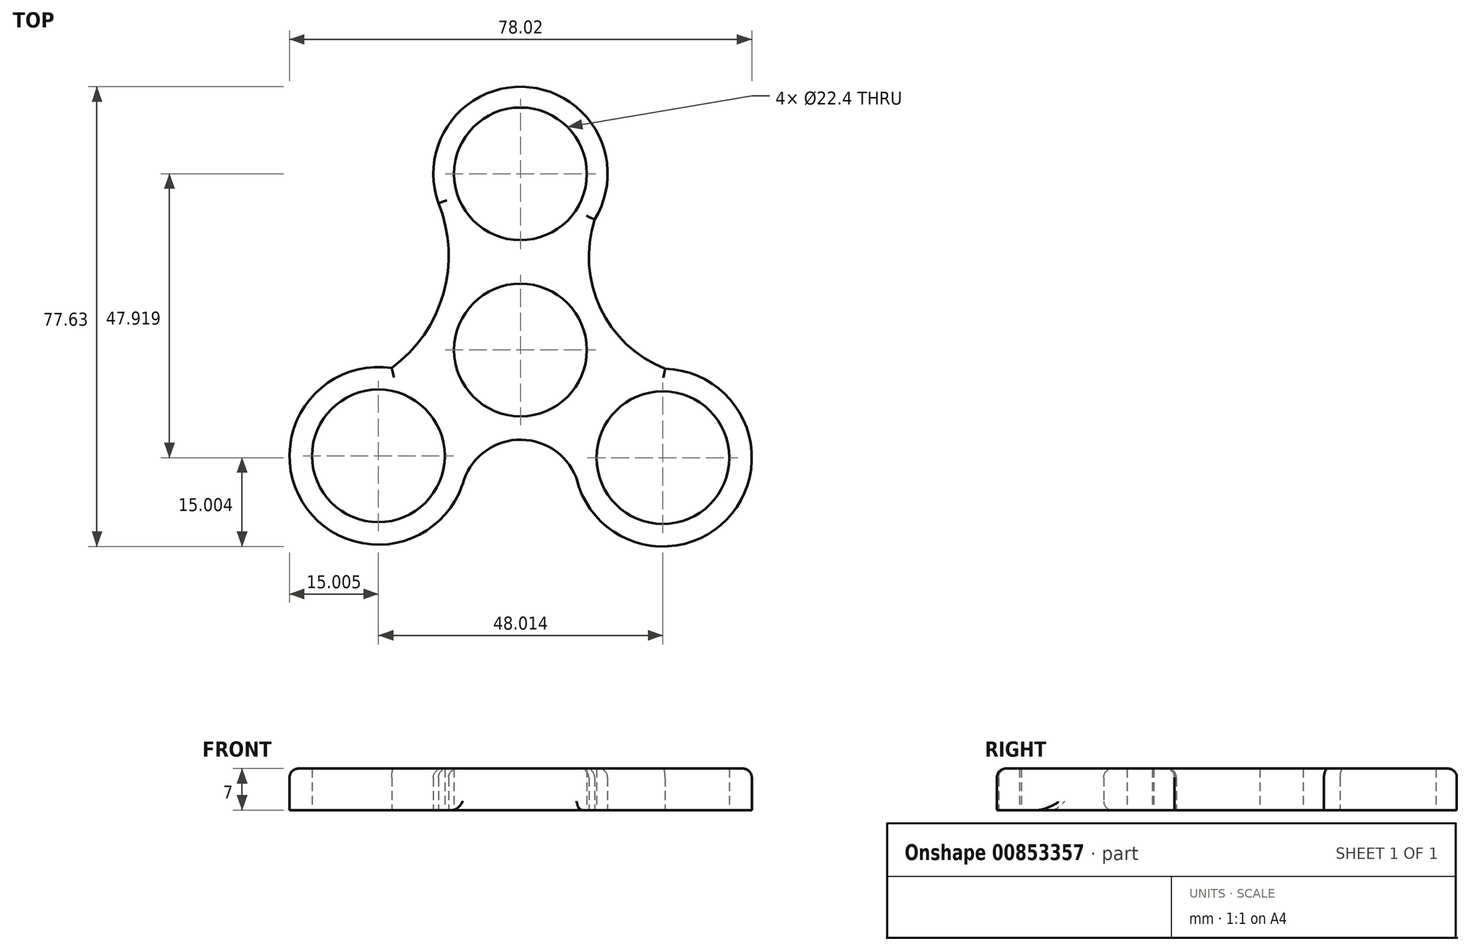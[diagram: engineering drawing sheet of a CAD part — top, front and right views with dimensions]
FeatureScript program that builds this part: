
annotation { "Feature Type Name" : "Feature", "Feature Type Description" : "" }
export const myFeature = defineFeature(function(context is Context, id is Id, definition is map)
    precondition{}
    {
        {
            var Q0;
            Q0=qCreatedBy(makeId("Top.planeOp"),FACE);
            var sketch = newSketch(context, id + "F0", { "sketchPlane" : qUnion([Q0])});
            skCircle(sketch, "E0", {"center": v(0, 0) * mm, "radius": 11.2 * mm});
            skCircle(sketch, "E1", {"center": v(0, 29.74) * mm, "radius": 11.2 * mm});
            skArc(sketch, "E2", {"start": v(12.52, 22.03) * mm, "mid": v(1.17, 44.4) * mm, "end": v(-13.58, 24.11) * mm});
            skCircle(sketch, "E3", {"center": v(-23.98, -17.88) * mm, "radius": 11.2 * mm});
            skCircle(sketch, "E4", {"center": v(24.04, -18.18) * mm, "radius": 11.2 * mm});
            skArc(sketch, "E5", {"start": v(9.44, -21.6) * mm, "mid": v(35.68, -27.64) * mm, "end": v(24.41, -3.18) * mm});
            skArc(sketch, "E6", {"start": v(12.52, 22.03) * mm, "mid": v(13.49, 7.07) * mm, "end": v(24.41, -3.18) * mm});
            skArc(sketch, "E7", {"start": v(-21.73, -3.05) * mm, "mid": v(-13.02, 9.5) * mm, "end": v(-13.84, 24.76) * mm});
            skArc(sketch, "E8", {"start": v(9.44, -21.6) * mm, "mid": v(-0.6, -15.17) * mm, "end": v(-9.79, -22.74) * mm});
            skArc(sketch, "E9.trimOffspring", {"start": v(-21.73, -3.05) * mm, "mid": v(-36.55, -26.06) * mm, "end": v(-9.5, -21.83) * mm});
            skSolve(sketch);
        }
        {
            var Q0;
            Q0=makeQuery(id+"F0.imprint","IMPRINT",FACE,{"disambiguationData":[TD([[makeQuery(id+"F0.imprint","IMPRINT",EDGE,{"derivedFrom":sQuery(id+"F0.wireOp",EDGE,"E0")}),-1.0]])]});
            extrude(context, id + "F1", {"entities" : qUnion([Q0]), "depth" : 7 * mm, "offsetDistance" : 25 * mm});
        }
        {
            var Q0;
            Q0=makeQuery(id+"F1.opExtrude","SWEPT_FACE",FACE,{"disambiguationData":[OSD([sQuery(id+"F0.wireOp",EDGE,"E8")])]});
            var Q1;
            Q1=makeQuery(id+"F1.opExtrude","CAP_EDGE",EDGE,{"disambiguationData":[OSD([sQuery(id+"F0.wireOp",EDGE,"E9.trimOffspring")])],"isStart":false});
            var Q2;
            Q2=makeQuery(id+"F1.opExtrude","CAP_EDGE",EDGE,{"disambiguationData":[OSD([sQuery(id+"F0.wireOp",EDGE,"E7")])],"isStart":false});
            var Q3;
            Q3=makeQuery(id+"F1.opExtrude","CAP_EDGE",EDGE,{"disambiguationData":[OSD([sQuery(id+"F0.wireOp",EDGE,"E2")])],"isStart":false});
            var Q4;
            Q4=makeQuery(id+"F1.opExtrude","CAP_EDGE",EDGE,{"disambiguationData":[OSD([sQuery(id+"F0.wireOp",EDGE,"E6")])],"isStart":false});
            var Q5;
            Q5=makeQuery(id+"F1.opExtrude","CAP_EDGE",EDGE,{"disambiguationData":[OSD([sQuery(id+"F0.wireOp",EDGE,"E5")])],"isStart":false});
            fillet(context, id + "F2", {"entities" : qUnion([Q0, Q1, Q2, Q3, Q4, Q5]), "radius" : 1.5 * mm, "tangentPropagation" : true, "allowEdgeOverflow" : false});
        }
    });
